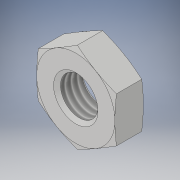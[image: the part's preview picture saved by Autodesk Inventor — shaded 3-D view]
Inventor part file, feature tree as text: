
AUTODESK INVENTOR PART (.ipt)
format: ipt  version: 2018 (Build 220112000, 112)  size: 180,736 bytes
history: native  units: in
note: dims shown in document units (in); Inventor stores cm internally (conversion verified against a paired STEP export)
features: other x70, sketch x3, revolve x2, extrude x1, thread x1
ambient origin geometry x8: Origin, YZ Plane, XZ Plane, XY Plane, X Axis, Y Axis, Z Axis, Center Point
bodies: Solid1 (feature_tree)
feature tree (77):
  sketch  "Sketch_8"  dims[d0=360.0deg d1=0.16in d2=0.0in]
  sketch  "Sketch_10"  dims[d3=360.0deg d4=0.1213in d5=0.0in]
  revolve  "Revolution1"  [1 undecoded]
  extrude  "Extrusion1"  Depth=0.1213in TaperAngle=0.0deg
  revolve  "Revolution2"  [1 undecoded]
  thread  "Thread1"  [1 undecoded]
  other  "NUT_XY"
  other  "NUT_YZ"
  other  "NUT_ZX"
  other  "NUT_X"
  other  "NUT_Y"
  other  "NUT_Z"
  other  "NUT_Center"
  other  "a1_XY"
  other  "a1_YZ"
  other  "a1_ZX"
  other  "a1_X"
  other  "a1_Y"
  other  "a1_Z"
  other  "a1_Center"
  other  "a2_XY"
  other  "a2_YZ"
  other  "a2_ZX"
  other  "a2_X"
  other  "a2_Y"
  other  "a2_Z"
  other  "a2_Center"
  other  "b1_XY"
  other  "b1_YZ"
  other  "b1_ZX"
  other  "b1_X"
  other  "b1_Y"
  other  "b1_Z"
  other  "b1_Center"
  other  "b2_XY"
  other  "b2_YZ"
  other  "b2_ZX"
  other  "b2_X"
  other  "b2_Y"
  other  "b2_Z"
  other  "b2_Center"
  other  "e_XY"
  other  "e_YZ"
  other  "e_ZX"
  other  "e_X"
  other  "e_Y"
  other  "e_Z"
  other  "e_Center"
  other  "ol1_XY"
  other  "ol1_YZ"
  other  "ol1_ZX"
  other  "ol1_X"
  other  "ol1_Y"
  other  "ol1_Z"
  other  "ol1_Center"
  other  "ol2_XY"
  other  "ol2_YZ"
  other  "ol2_ZX"
  other  "ol2_X"
  other  "ol2_Y"
  other  "ol2_Z"
  other  "ol2_Center"
  other  "th1_XY"
  other  "th1_YZ"
  other  "th1_ZX"
  other  "th1_X"
  other  "th1_Y"
  other  "th1_Z"
  other  "th1_Center"
  other  "th2_XY"
  other  "th2_YZ"
  other  "th2_ZX"
  other  "th2_X"
  other  "th2_Y"
  other  "th2_Z"
  other  "th2_Center"
  sketch  "Sketch_11"  dims[d6=0.0in d7=0.0in d8=0.0in]
note: 3 required parameter values undecoded (feature->parameter linkage not recoverable at this tier; creation-order binding heuristic only, values carry confidence <= 0.55)